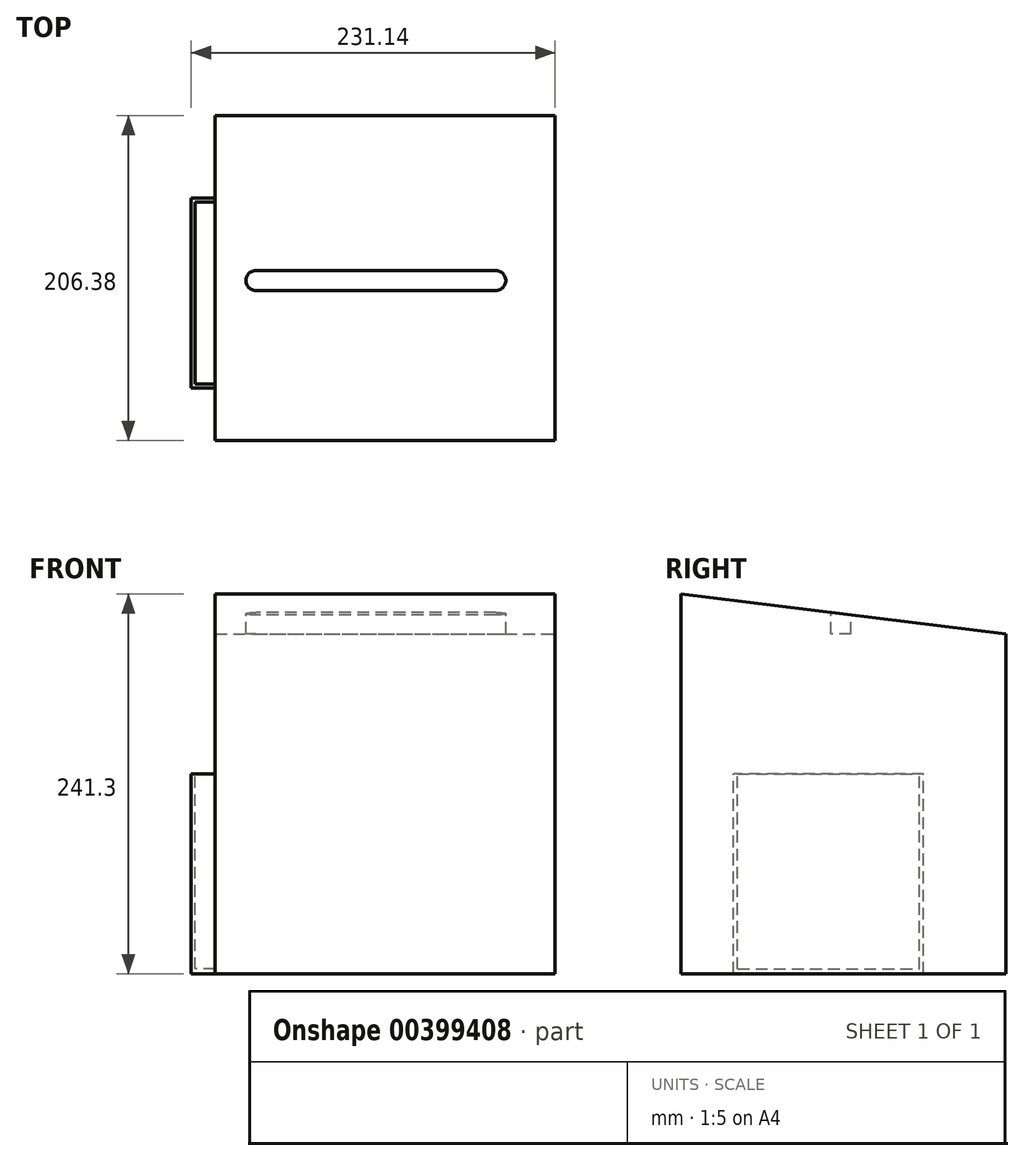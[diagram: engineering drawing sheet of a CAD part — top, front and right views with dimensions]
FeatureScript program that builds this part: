
annotation { "Feature Type Name" : "Feature", "Feature Type Description" : "" }
export const myFeature = defineFeature(function(context is Context, id is Id, definition is map)
    precondition{}
    {
        {
            var Q0;
            Q0=qCreatedBy(makeId("Front.planeOp"),FACE);
            var sketch = newSketch(context, id + "F0", { "sketchPlane" : qUnion([Q0])});
            skLineSegment(sketch, "E0.bottom", {"start": v(-93.8, 125.7) * mm, "end": v(122.1, 125.7) * mm});
            skLineSegment(sketch, "E0.top", {"start": v(-93.8, -115.6) * mm, "end": v(122.1, -115.6) * mm});
            skLineSegment(sketch, "E0.left", {"start": v(-93.8, 125.7) * mm, "end": v(-93.8, -115.6) * mm});
            skLineSegment(sketch, "E0.right", {"start": v(122.1, 125.7) * mm, "end": v(122.1, -115.6) * mm});
            skSolve(sketch);
        }
        {
            var Q0;
            Q0=makeQuery(id+"F0.imprint","IMPRINT",FACE,{"disambiguationData":[TD([[makeQuery(id+"F0.imprint","IMPRINT",EDGE,{"derivedFrom":sQuery(id+"F0.wireOp",EDGE,"E0.bottom")}),-1.0]])]});
            extrude(context, id + "F1", {"entities" : qUnion([Q0]), "depth" : 206.38 * mm});
        }
        {
            var Q0;
            Q0=makeQuery(id+"F1.opExtrude","SWEPT_FACE",FACE,{"disambiguationData":[OSD([sQuery(id+"F0.wireOp",EDGE,"E0.bottom")])]});
            cPlane(context, id + "F2", {"entities" : qUnion([Q0]), "cplaneType" : CPlaneType.OFFSET, "offset" : 0 * mm, "width" : 152.4 * mm, "height" : 152.4 * mm});
        }
        {
            var Q0;
            Q0=qCreatedBy(id+"F2.planeOp",FACE);
            var sketch = newSketch(context, id + "F3", { "sketchPlane" : qUnion([Q0])});
            skLineSegment(sketch, "E1.bottom", {"start": v(-68, -98.43) * mm, "end": v(84.4, -98.42) * mm});
            skLineSegment(sketch, "E1.top", {"start": v(-68, -111.13) * mm, "end": v(84.4, -111.12) * mm});
            skLineSegment(sketch, "E1.left", {"start": v(-68, -98.43) * mm, "end": v(-68, -111.13) * mm});
            skLineSegment(sketch, "E1.right", {"start": v(84.4, -98.42) * mm, "end": v(84.4, -111.12) * mm});
            skCircle(sketch, "E2", {"center": v(-68, -104.78) * mm, "radius": 6.35 * mm});
            skCircle(sketch, "E3", {"center": v(84.4, -104.77) * mm, "radius": 6.35 * mm});
            skSolve(sketch);
        }
        {
            var Q0;
            {var subQ0=sQuery(id+"F3.wireOp",EDGE,"E1.bottom");Q0=makeQuery(id+"F3.imprint","IMPRINT",FACE,{"disambiguationData":[TD([[makeQuery(id+"F3.imprint","IMPRINT",EDGE,{"derivedFrom":subQ0}),-1.0]])]});}
            var Q1;
            {var subQ0=sQuery(id+"F3.wireOp",EDGE,"E1.left");Q1=makeQuery(id+"F3.imprint","IMPRINT",FACE,{"disambiguationData":[TD([[makeQuery(id+"F3.imprint","IMPRINT",EDGE,{"derivedFrom":subQ0}),-1.0]])]});}
            var Q2;
            {var subQ0=sQuery(id+"F3.wireOp",EDGE,"E1.left");Q2=makeQuery(id+"F3.imprint","IMPRINT",FACE,{"disambiguationData":[TD([[makeQuery(id+"F3.imprint","IMPRINT",EDGE,{"derivedFrom":subQ0}),1.0]])]});}
            var Q3;
            {var subQ0=sQuery(id+"F3.wireOp",EDGE,"E1.right");Q3=makeQuery(id+"F3.imprint","IMPRINT",FACE,{"disambiguationData":[TD([[makeQuery(id+"F3.imprint","IMPRINT",EDGE,{"derivedFrom":subQ0}),1.0]])]});}
            var Q4;
            {var subQ0=sQuery(id+"F3.wireOp",EDGE,"E1.right");Q4=makeQuery(id+"F3.imprint","IMPRINT",FACE,{"disambiguationData":[TD([[makeQuery(id+"F3.imprint","IMPRINT",EDGE,{"derivedFrom":subQ0}),-1.0]])]});}
            extrude(context, id + "F4", {"entities" : qUnion([Q0, Q1, Q2, Q3, Q4]), "operationType" : NewBodyOperationType.REMOVE, "oppositeDirection" : true, "depth" : 25.4 * mm});
        }
        {
            var Q0;
            Q0=qCreatedBy(makeId("Right.planeOp"),FACE);
            var sketch = newSketch(context, id + "F5", { "sketchPlane" : qUnion([Q0])});
            skLineSegment(sketch, "E4", {"start": v(0, 100.3) * mm, "end": v(-206.38, 125.7) * mm});
            skLineSegment(sketch, "E5", {"start": v(-206.38, 125.7) * mm, "end": v(13.32, 125.7) * mm});
            skLineSegment(sketch, "E6", {"start": v(13.32, 125.7) * mm, "end": v(13.32, 98.04) * mm});
            skLineSegment(sketch, "E7", {"start": v(13.32, 98.04) * mm, "end": v(0, 100.3) * mm});
            skSolve(sketch);
        }
        {
            var Q0;
            Q0=makeQuery(id+"F5.imprint","IMPRINT",FACE,{"disambiguationData":[TD([[makeQuery(id+"F5.imprint","IMPRINT",EDGE,{"derivedFrom":sQuery(id+"F5.wireOp",EDGE,"E4")}),-1.0]])]});
            extrude(context, id + "F6", {"entities" : qUnion([Q0]), "operationType" : NewBodyOperationType.REMOVE, "oppositeDirection" : true, "depth" : 197.36 * mm, "hasSecondDirection" : true, "secondDirectionOppositeDirection" : false, "secondDirectionDepth" : 177.8 * mm});
        }
        {
            var Q0;
            Q0=makeQuery(id+"F1.opExtrude","SWEPT_FACE",FACE,{"disambiguationData":[OSD([sQuery(id+"F0.wireOp",EDGE,"E0.left")])]});
            cPlane(context, id + "F7", {"entities" : qUnion([Q0]), "cplaneType" : CPlaneType.OFFSET, "offset" : 0 * mm, "width" : 152.4 * mm, "height" : 152.4 * mm});
        }
        {
            var Q0;
            Q0=qCreatedBy(id+"F7.planeOp",FACE);
            var sketch = newSketch(context, id + "F8", { "sketchPlane" : qUnion([Q0])});
            skLineSegment(sketch, "E8.bottom", {"start": v(52.42, -115.6) * mm, "end": v(173.07, -115.6) * mm});
            skLineSegment(sketch, "E8.top", {"start": v(52.42, 11.4) * mm, "end": v(173.07, 11.4) * mm});
            skLineSegment(sketch, "E8.left", {"start": v(52.42, -115.6) * mm, "end": v(52.42, 11.4) * mm});
            skLineSegment(sketch, "E8.right", {"start": v(173.07, -115.6) * mm, "end": v(173.07, 11.4) * mm});
            skSolve(sketch);
        }
        {
            var Q0;
            Q0=makeQuery(id+"F8.imprint","IMPRINT",FACE,{"disambiguationData":[TD([[makeQuery(id+"F8.imprint","IMPRINT",EDGE,{"derivedFrom":sQuery(id+"F8.wireOp",EDGE,"E8.bottom")}),1.0]])]});
            extrude(context, id + "F9", {"entities" : qUnion([Q0]), "depth" : 15.24 * mm});
        }
        {
            var Q0;
            Q0=makeQuery(id+"F9.opExtrude","SWEPT_FACE",FACE,{"disambiguationData":[OSD([sQuery(id+"F8.wireOp",EDGE,"E8.top")])]});
            cPlane(context, id + "F10", {"entities" : qUnion([Q0]), "cplaneType" : CPlaneType.OFFSET, "offset" : 0 * mm, "width" : 152.4 * mm, "height" : 152.4 * mm});
        }
        {
            var Q0;
            Q0=qCreatedBy(id+"F10.planeOp",FACE);
            var sketch = newSketch(context, id + "F11", { "sketchPlane" : qUnion([Q0])});
            skLineSegment(sketch, "E9.bottom", {"start": v(-93.8, -170.53) * mm, "end": v(-106.5, -170.53) * mm});
            skLineSegment(sketch, "E9.top", {"start": v(-93.8, -54.96) * mm, "end": v(-106.5, -54.96) * mm});
            skLineSegment(sketch, "E9.left", {"start": v(-93.8, -170.53) * mm, "end": v(-93.8, -54.96) * mm});
            skLineSegment(sketch, "E9.right", {"start": v(-106.5, -170.53) * mm, "end": v(-106.5, -54.96) * mm});
            skSolve(sketch);
        }
        {
            var Q0;
            Q0=makeQuery(id+"F11.imprint","IMPRINT",FACE,{"disambiguationData":[TD([[makeQuery(id+"F11.imprint","IMPRINT",EDGE,{"derivedFrom":sQuery(id+"F11.wireOp",EDGE,"E9.bottom")}),-1.0]])]});
            extrude(context, id + "F12", {"entities" : qUnion([Q0]), "operationType" : NewBodyOperationType.REMOVE, "oppositeDirection" : true, "depth" : 123.95 * mm});
        }
    });
